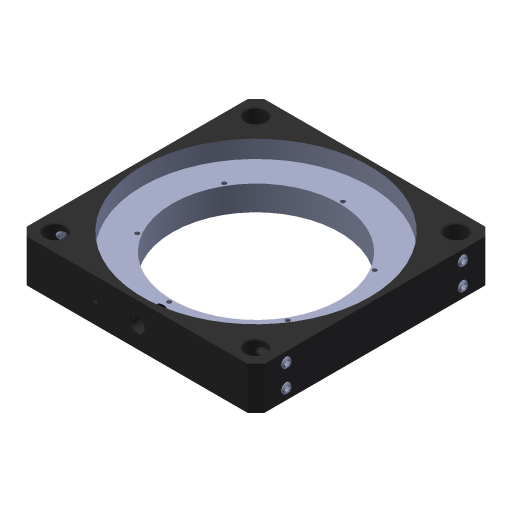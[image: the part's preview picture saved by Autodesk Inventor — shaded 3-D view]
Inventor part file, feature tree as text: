
AUTODESK INVENTOR PART (.ipt)
format: ipt  version: 2023 (Build 270158000, 158)  size: 398,336 bytes
history: native  units: mm
features: other x10, imported_body x9, sketch x3, extrude x2, hole x1, projected_geometry x1
ambient origin geometry x8: Origin, YZ Plane, XZ Plane, XY Plane, X Axis, Y Axis, Z Axis, Center Point
bodies: Body1 (feature_tree), Body2 (feature_tree), Body3 (feature_tree), Body4 (feature_tree), Body5 (feature_tree), Body6 (feature_tree), Body7 (feature_tree), Body8 (feature_tree), Body9 (feature_tree)
feature tree (26):
  other  "13108-001-1-solid1"
  other  "13108-E0W1"
  extrude  "Extrusion1"  Depth=5.25mm TaperAngle=0.0deg
  extrude  "Extrusion2"  Depth=4.0mm TaperAngle=0.0deg
  hole  "Hole2"  [1 undecoded]
  other  "SS4S019-1-1-solid1"
  other  "SS4S019-1-2-solid1"
  other  "SS4S019-1-3-solid1"
  other  "SS4S019-1-4-solid1"
  other  "SS4S019-1-5-solid1"
  other  "SS4S019-1-6-solid1"
  other  "SS4S019-1-7-solid1"
  other  "SS4S019-1-8-solid1"
  imported_body  "Base1"
  imported_body  "Base2"
  imported_body  "Base3"
  imported_body  "Base4"
  imported_body  "Base5"
  imported_body  "Base6"
  imported_body  "Base7"
  imported_body  "Base8"
  imported_body  "Base9"
  sketch  "Sketch1"  dims[d1=68.0mm d2=5.25mm d3=0.0mm]
  projected_geometry  "Projected Loop1"
  sketch  "Sketch2"  dims[d4=50.0mm d5=4.0mm d6=0.0mm]
  sketch  "Sketch4"  dims[d16=26.0mm d17=60.0mm d19=360.0deg d21=1.321114mm d22=3.4mm d23=11.5mm d24=7.0mm d25=90.0deg d26=8.0mm d27=20.594885mm]
note: 1 required parameter value undecoded (feature->parameter linkage not recoverable at this tier; creation-order binding heuristic only, values carry confidence <= 0.55)
